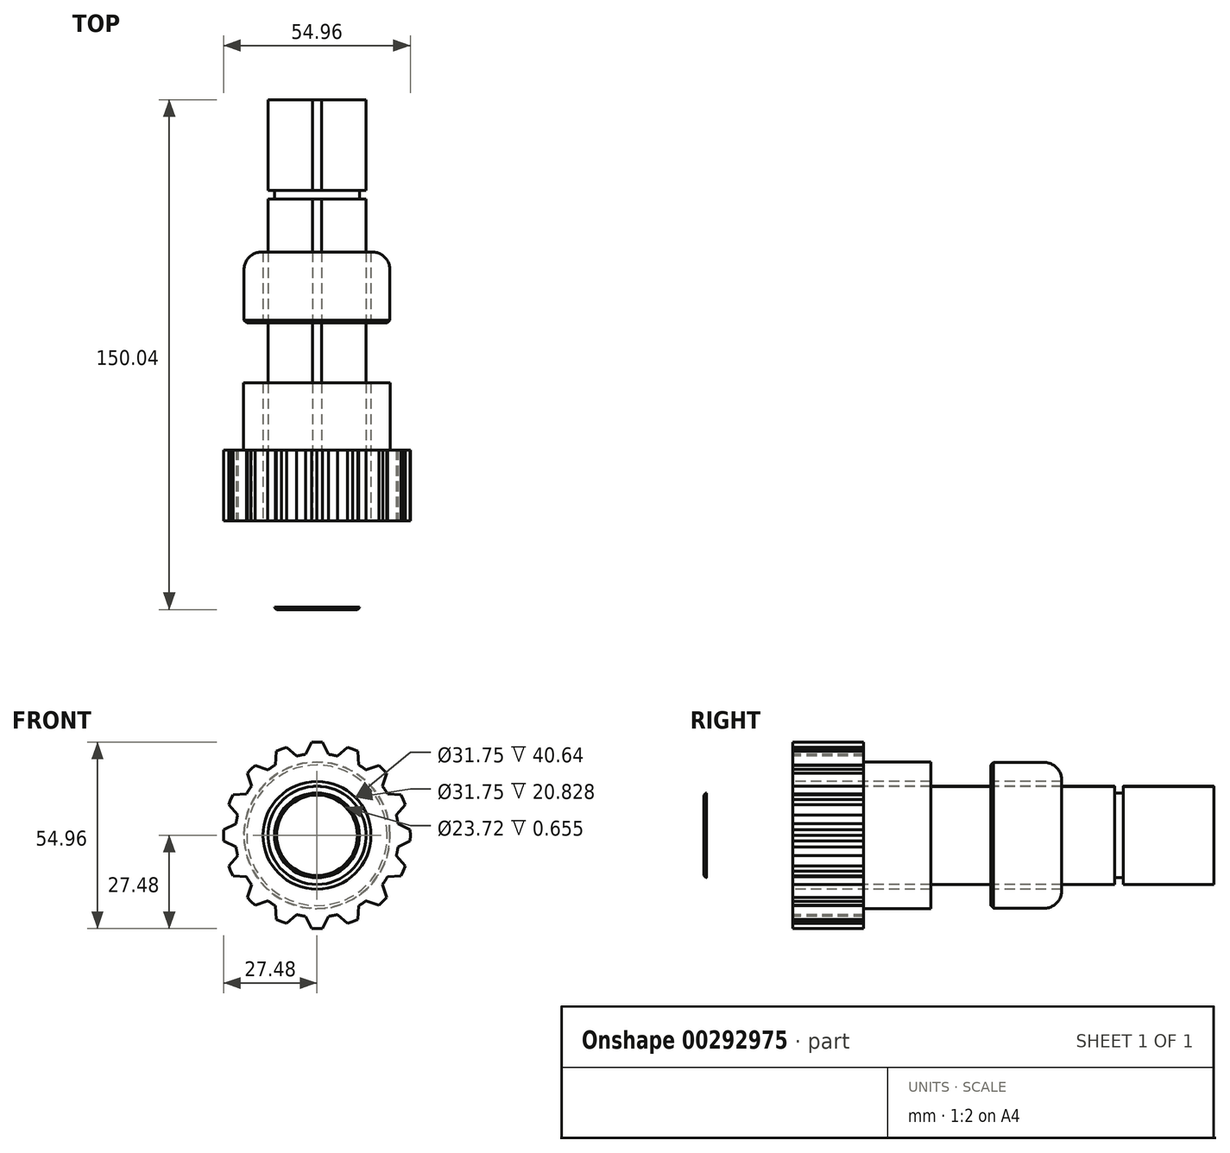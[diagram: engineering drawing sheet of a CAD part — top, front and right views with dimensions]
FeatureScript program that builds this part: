
annotation { "Feature Type Name" : "Feature", "Feature Type Description" : "" }
export const myFeature = defineFeature(function(context is Context, id is Id, definition is map)
    precondition{}
    {
        {
            var Q0;
            Q0=qCreatedBy(makeId("Front.planeOp"),FACE);
            var sketch = newSketch(context, id + "F0", { "sketchPlane" : qUnion([Q0])});
            skCircle(sketch, "E0", {"center": v(0, 0) * mm, "radius": 12.5 * mm});
            skCircle(sketch, "E1", {"center": v(0, 0) * mm, "radius": 15.88 * mm});
            skCircle(sketch, "E2", {"center": v(0, 0) * mm, "radius": 21.46 * mm});
            skCircle(sketch, "E3", {"center": v(0, 0) * mm, "radius": 11.86 * mm});
            skLineSegment(sketch, "E4", {"start": v(0, 15.88) * mm, "end": v(0, 14.45) * mm});
            skCircle(sketch, "E5", {"center": v(0, 0) * mm, "radius": 14.45 * mm});
            skPoint(sketch, "E6", {"position": v(-0.58, 15.85) * mm});
            skPoint(sketch, "E7", {"position": v(-1.3, 14.4) * mm});
            skPoint(sketch, "E8", {"position": v(1.3, 14.4) * mm});
            skPoint(sketch, "E9", {"position": v(0.58, 15.85) * mm});
            skLineSegment(sketch, "E10", {"start": v(-1.3, 14.4) * mm, "end": v(-0.58, 15.85) * mm});
            skLineSegment(sketch, "E11", {"start": v(1.3, 14.4) * mm, "end": v(0.58, 15.85) * mm});
            skLineSegment(sketch, "E12.1.0", {"start": v(-3.41, 15.5) * mm, "end": v(-3.1, 14.11) * mm});
            skLineSegment(sketch, "E12.1.1", {"start": v(-4.36, 13.78) * mm, "end": v(-3.98, 15.35) * mm});
            skLineSegment(sketch, "E12.1.2", {"start": v(-1.83, 14.34) * mm, "end": v(-2.84, 15.6) * mm});
            skLineSegment(sketch, "E12.2.0", {"start": v(-6.67, 14.4) * mm, "end": v(-6.07, 13.12) * mm});
            skLineSegment(sketch, "E12.2.1", {"start": v(-7.22, 12.52) * mm, "end": v(-7.19, 14.14) * mm});
            skLineSegment(sketch, "E12.2.2", {"start": v(-4.87, 13.6) * mm, "end": v(-6.12, 14.63) * mm});
            skLineSegment(sketch, "E13.2.3.0", {"start": v(-9.6, 12.64) * mm, "end": v(-8.75, 11.5) * mm});
            skLineSegment(sketch, "E13.3.3.0", {"start": v(-9.74, 10.67) * mm, "end": v(-10.06, 12.26) * mm});
            skLineSegment(sketch, "E13.6.3.0", {"start": v(-7.68, 12.25) * mm, "end": v(-9.13, 12.97) * mm});
            skLineSegment(sketch, "E13.2.4.0", {"start": v(-12.1, 10.28) * mm, "end": v(-11.02, 9.36) * mm});
            skLineSegment(sketch, "E13.3.4.0", {"start": v(-11.81, 8.33) * mm, "end": v(-12.46, 9.82) * mm});
            skLineSegment(sketch, "E13.6.4.0", {"start": v(-10.13, 10.3) * mm, "end": v(-11.7, 10.7) * mm});
            skLineSegment(sketch, "E13.2.5.0", {"start": v(-14.03, 7.44) * mm, "end": v(-12.77, 6.77) * mm});
            skLineSegment(sketch, "E13.3.5.0", {"start": v(-13.33, 5.6) * mm, "end": v(-14.28, 6.9) * mm});
            skLineSegment(sketch, "E13.6.5.0", {"start": v(-12.1, 7.89) * mm, "end": v(-13.73, 7.94) * mm});
            skLineSegment(sketch, "E13.2.6.0", {"start": v(-15.3, 4.25) * mm, "end": v(-13.93, 3.87) * mm});
            skLineSegment(sketch, "E13.3.6.0", {"start": v(-14.22, 2.6) * mm, "end": v(-15.43, 3.68) * mm});
            skLineSegment(sketch, "E13.6.6.0", {"start": v(-13.52, 5.1) * mm, "end": v(-15.12, 4.8) * mm});
            skLineSegment(sketch, "E13.2.7.0", {"start": v(-15.85, 0.86) * mm, "end": v(-14.43, 0.78) * mm});
            skLineSegment(sketch, "E13.3.7.0", {"start": v(-14.44, -0.52) * mm, "end": v(-15.86, 0.27) * mm});
            skLineSegment(sketch, "E13.6.7.0", {"start": v(-14.3, 2.08) * mm, "end": v(-15.8, 1.44) * mm});
            skLineSegment(sketch, "E13.2.8.0", {"start": v(-15.67, -2.57) * mm, "end": v(-14.26, -2.34) * mm});
            skLineSegment(sketch, "E13.3.8.0", {"start": v(-14, -3.61) * mm, "end": v(-15.55, -3.14) * mm});
            skLineSegment(sketch, "E13.6.8.0", {"start": v(-14.41, -1.05) * mm, "end": v(-15.74, -1.99) * mm});
            skLineSegment(sketch, "E13.2.9.0", {"start": v(-14.75, -5.88) * mm, "end": v(-13.43, -5.35) * mm});
            skLineSegment(sketch, "E13.3.9.0", {"start": v(-12.9, -6.53) * mm, "end": v(-14.5, -6.4) * mm});
            skLineSegment(sketch, "E13.6.9.0", {"start": v(-13.85, -4.12) * mm, "end": v(-14.94, -5.32) * mm});
            skLineSegment(sketch, "E13.2.10.0", {"start": v(-13.14, -8.9) * mm, "end": v(-11.96, -8.11) * mm});
            skLineSegment(sketch, "E13.3.10.0", {"start": v(-11.19, -9.15) * mm, "end": v(-12.8, -9.38) * mm});
            skLineSegment(sketch, "E13.6.10.0", {"start": v(-12.64, -7) * mm, "end": v(-13.45, -8.41) * mm});
            skLineSegment(sketch, "E13.2.11.0", {"start": v(-10.92, -11.53) * mm, "end": v(-9.94, -10.5) * mm});
            skLineSegment(sketch, "E13.3.11.0", {"start": v(-8.96, -11.34) * mm, "end": v(-10.48, -11.9) * mm});
            skLineSegment(sketch, "E13.6.11.0", {"start": v(-10.84, -9.56) * mm, "end": v(-11.32, -11.1) * mm});
            skLineSegment(sketch, "E13.2.12.0", {"start": v(-8.18, -13.6) * mm, "end": v(-7.45, -12.38) * mm});
            skLineSegment(sketch, "E13.3.12.0", {"start": v(-6.3, -13) * mm, "end": v(-7.67, -13.88) * mm});
            skLineSegment(sketch, "E13.6.12.0", {"start": v(-8.53, -11.66) * mm, "end": v(-8.67, -13.28) * mm});
            skLineSegment(sketch, "E13.2.13.0", {"start": v(-5.07, -15.04) * mm, "end": v(-4.61, -13.7) * mm});
            skLineSegment(sketch, "E13.3.13.0", {"start": v(-3.37, -14.06) * mm, "end": v(-4.5, -15.2) * mm});
            skLineSegment(sketch, "E13.6.13.0", {"start": v(-5.83, -13.23) * mm, "end": v(-5.61, -14.83) * mm});
            skLineSegment(sketch, "E13.2.14.0", {"start": v(-1.72, -15.78) * mm, "end": v(-1.56, -14.37) * mm});
            skLineSegment(sketch, "E13.3.14.0", {"start": v(-0.27, -14.45) * mm, "end": v(-1.13, -15.82) * mm});
            skLineSegment(sketch, "E13.6.14.0", {"start": v(-2.85, -14.17) * mm, "end": v(-2.3, -15.7) * mm});
            skLineSegment(sketch, "E13.2.15.0", {"start": v(1.72, -15.78) * mm, "end": v(1.56, -14.37) * mm});
            skLineSegment(sketch, "E13.3.15.0", {"start": v(2.85, -14.17) * mm, "end": v(2.3, -15.7) * mm});
            skLineSegment(sketch, "E13.6.15.0", {"start": v(0.27, -14.45) * mm, "end": v(1.13, -15.82) * mm});
            skLineSegment(sketch, "E13.2.16.0", {"start": v(5.07, -15.04) * mm, "end": v(4.61, -13.7) * mm});
            skLineSegment(sketch, "E13.3.16.0", {"start": v(5.83, -13.23) * mm, "end": v(5.61, -14.83) * mm});
            skLineSegment(sketch, "E13.6.16.0", {"start": v(3.37, -14.06) * mm, "end": v(4.5, -15.2) * mm});
            skLineSegment(sketch, "E13.2.17.0", {"start": v(8.18, -13.6) * mm, "end": v(7.45, -12.38) * mm});
            skLineSegment(sketch, "E13.3.17.0", {"start": v(8.53, -11.66) * mm, "end": v(8.67, -13.28) * mm});
            skLineSegment(sketch, "E13.6.17.0", {"start": v(6.3, -13) * mm, "end": v(7.67, -13.88) * mm});
            skLineSegment(sketch, "E13.2.18.0", {"start": v(10.92, -11.53) * mm, "end": v(9.94, -10.5) * mm});
            skLineSegment(sketch, "E13.3.18.0", {"start": v(10.84, -9.56) * mm, "end": v(11.32, -11.1) * mm});
            skLineSegment(sketch, "E13.6.18.0", {"start": v(8.96, -11.34) * mm, "end": v(10.48, -11.9) * mm});
            skLineSegment(sketch, "E13.2.19.0", {"start": v(13.14, -8.9) * mm, "end": v(11.96, -8.11) * mm});
            skLineSegment(sketch, "E13.3.19.0", {"start": v(12.64, -7) * mm, "end": v(13.45, -8.41) * mm});
            skLineSegment(sketch, "E13.6.19.0", {"start": v(11.19, -9.15) * mm, "end": v(12.8, -9.38) * mm});
            skLineSegment(sketch, "E13.2.20.0", {"start": v(14.75, -5.88) * mm, "end": v(13.43, -5.35) * mm});
            skLineSegment(sketch, "E13.3.20.0", {"start": v(13.85, -4.12) * mm, "end": v(14.94, -5.32) * mm});
            skLineSegment(sketch, "E13.6.20.0", {"start": v(12.9, -6.53) * mm, "end": v(14.5, -6.4) * mm});
            skLineSegment(sketch, "E13.2.21.0", {"start": v(15.67, -2.57) * mm, "end": v(14.26, -2.34) * mm});
            skLineSegment(sketch, "E13.3.21.0", {"start": v(14.41, -1.05) * mm, "end": v(15.74, -1.99) * mm});
            skLineSegment(sketch, "E13.6.21.0", {"start": v(14, -3.61) * mm, "end": v(15.55, -3.14) * mm});
            skLineSegment(sketch, "E13.2.22.0", {"start": v(15.85, 0.86) * mm, "end": v(14.43, 0.78) * mm});
            skLineSegment(sketch, "E13.3.22.0", {"start": v(14.3, 2.08) * mm, "end": v(15.8, 1.44) * mm});
            skLineSegment(sketch, "E13.6.22.0", {"start": v(14.44, -0.52) * mm, "end": v(15.86, 0.27) * mm});
            skLineSegment(sketch, "E13.2.23.0", {"start": v(15.3, 4.25) * mm, "end": v(13.93, 3.87) * mm});
            skLineSegment(sketch, "E13.3.23.0", {"start": v(13.52, 5.1) * mm, "end": v(15.12, 4.8) * mm});
            skLineSegment(sketch, "E13.6.23.0", {"start": v(14.22, 2.6) * mm, "end": v(15.43, 3.68) * mm});
            skLineSegment(sketch, "E13.2.24.0", {"start": v(14.03, 7.44) * mm, "end": v(12.77, 6.77) * mm});
            skLineSegment(sketch, "E13.3.24.0", {"start": v(12.1, 7.89) * mm, "end": v(13.73, 7.94) * mm});
            skLineSegment(sketch, "E13.6.24.0", {"start": v(13.33, 5.6) * mm, "end": v(14.28, 6.9) * mm});
            skLineSegment(sketch, "E13.2.25.0", {"start": v(12.1, 10.28) * mm, "end": v(11.02, 9.36) * mm});
            skLineSegment(sketch, "E13.3.25.0", {"start": v(10.13, 10.3) * mm, "end": v(11.7, 10.7) * mm});
            skLineSegment(sketch, "E13.6.25.0", {"start": v(11.81, 8.33) * mm, "end": v(12.46, 9.82) * mm});
            skLineSegment(sketch, "E13.2.26.0", {"start": v(9.6, 12.64) * mm, "end": v(8.75, 11.5) * mm});
            skLineSegment(sketch, "E13.3.26.0", {"start": v(7.68, 12.25) * mm, "end": v(9.13, 12.97) * mm});
            skLineSegment(sketch, "E13.6.26.0", {"start": v(9.74, 10.67) * mm, "end": v(10.06, 12.26) * mm});
            skLineSegment(sketch, "E13.2.27.0", {"start": v(6.67, 14.4) * mm, "end": v(6.07, 13.12) * mm});
            skLineSegment(sketch, "E13.3.27.0", {"start": v(4.87, 13.6) * mm, "end": v(6.12, 14.63) * mm});
            skLineSegment(sketch, "E13.6.27.0", {"start": v(7.22, 12.52) * mm, "end": v(7.19, 14.14) * mm});
            skLineSegment(sketch, "E13.2.28.0", {"start": v(3.41, 15.5) * mm, "end": v(3.1, 14.11) * mm});
            skLineSegment(sketch, "E13.3.28.0", {"start": v(1.83, 14.34) * mm, "end": v(2.84, 15.6) * mm});
            skLineSegment(sketch, "E13.6.28.0", {"start": v(4.36, 13.78) * mm, "end": v(3.98, 15.35) * mm});
            skFitSpline(sketch, "E14", {"points": [v(-1.3, 14.4) * mm, v(0, 14.45) * mm, v(1.3, 14.4) * mm], "startDerivative": vector(2.6, 0.18) * mm, "endDerivative": vector(2.6, -0.18) * mm});
            skFitSpline(sketch, "E15", {"points": [v(-0.58, 15.85) * mm, v(0, 15.88) * mm, v(0.58, 15.85) * mm], "startDerivative": vector(1.17, 0.08) * mm, "endDerivative": vector(1.17, -0.08) * mm});
            skSolve(sketch);
        }
        {
            var Q0;
            Q0=makeQuery(id+"F0.imprint","IMPRINT",FACE,{"disambiguationData":[TD([[makeQuery(id+"F0.imprint","IMPRINT",EDGE,{"derivedFrom":sQuery(id+"F0.wireOp",EDGE,"E0")}),1.0]])]});
            extrude(context, id + "F1", {"entities" : qUnion([Q0]), "depth" : 26.21 * mm, "hasSecondDirection" : true, "secondDirectionOppositeDirection" : false, "secondDirectionDepth" : 25.4 * mm});
        }
        {
            var Q0;
            Q0=makeQuery(id+"F0.imprint","IMPRINT",FACE,{"disambiguationData":[TD([[makeQuery(id+"F0.imprint","IMPRINT",EDGE,{"derivedFrom":sQuery(id+"F0.wireOp",EDGE,"E0")}),1.0]])]});
            extrude(context, id + "F2", {"entities" : qUnion([Q0]), "operationType" : NewBodyOperationType.REMOVE, "depth" : 1.47 * mm});
        }
        {
            var Q0;
            Q0=makeQuery(id+"F0.imprint","IMPRINT",FACE,{"disambiguationData":[TD([[makeQuery(id+"F0.imprint","IMPRINT",EDGE,{"derivedFrom":sQuery(id+"F0.wireOp",EDGE,"E3")}),1.0]])]});
            var Q1;
            Q1=makeQuery(id+"F0.imprint","IMPRINT",FACE,{"disambiguationData":[TD([[makeQuery(id+"F0.imprint","IMPRINT",EDGE,{"derivedFrom":sQuery(id+"F0.wireOp",EDGE,"E0")}),1.0]])]});
            var Q2;
            Q2=makeQuery(id+"F0.imprint","IMPRINT",FACE,{"disambiguationData":[TD([[makeQuery(id+"F0.imprint","IMPRINT",EDGE,{"derivedFrom":sQuery(id+"F0.wireOp",EDGE,"E0")}),-1.0]])]});
            extrude(context, id + "F3", {"entities" : qUnion([Q0, Q1, Q2]), "operationType" : NewBodyOperationType.ADD, "oppositeDirection" : true, "depth" : 123.98 * mm});
        }
        {
            var Q0;
            Q0=makeQuery(id+"F0.imprint","IMPRINT",FACE,{"disambiguationData":[TD([[makeQuery(id+"F0.imprint","IMPRINT",EDGE,{"derivedFrom":sQuery(id+"F0.wireOp",EDGE,"E0")}),-1.0]])]});
            extrude(context, id + "F4", {"entities" : qUnion([Q0]), "operationType" : NewBodyOperationType.REMOVE, "oppositeDirection" : true, "depth" : 97.3 * mm, "hasSecondDirection" : true, "secondDirectionOppositeDirection" : true, "secondDirectionDepth" : 94.77 * mm});
        }
        {
            var Q0;
            Q0=makeQuery(id+"F0.imprint","IMPRINT",FACE,{"disambiguationData":[TD([[makeQuery(id+"F0.imprint","IMPRINT",EDGE,{"derivedFrom":sQuery(id+"F0.wireOp",EDGE,"E1")}),-1.0]])]});
            extrude(context, id + "F5", {"entities" : qUnion([Q0]), "operationType" : NewBodyOperationType.ADD, "oppositeDirection" : true, "depth" : 79.2 * mm, "hasSecondDirection" : true, "secondDirectionOppositeDirection" : true, "secondDirectionDepth" : 58.37 * mm});
        }
        {
            var Q0;
            Q0=makeQuery(id+"F1.opExtrude","CAP_EDGE",EDGE,{"disambiguationData":[OSD([sQuery(id+"F0.wireOp",EDGE,"E0")])],"isStart":false});
            chamfer(context, id + "F6", {"entities" : qUnion([Q0]), "width" : 0.8 * mm, "tangentPropagation" : true});
        }
        {
            var Q0;
            Q0=makeQuery(id+"F5.opExtrude","CAP_EDGE",EDGE,{"disambiguationData":[OSD([sQuery(id+"F0.wireOp",EDGE,"E2")])],"isStart":false});
            fillet(context, id + "F7", {"entities" : qUnion([Q0]), "radius" : 5.16 * mm, "tangentPropagation" : true, "allowEdgeOverflow" : false});
        }
        {
            var Q0;
            Q0=makeQuery(id+"F5.opExtrude","CAP_EDGE",EDGE,{"disambiguationData":[OSD([sQuery(id+"F0.wireOp",EDGE,"E2")])],"isStart":true});
            chamfer(context, id + "F8", {"entities" : qUnion([Q0]), "width" : 0.79 * mm, "tangentPropagation" : true});
        }
        {
            var Q0;
            Q0=qCreatedBy(makeId("Front.planeOp"),FACE);
            var sketch = newSketch(context, id + "F9", { "sketchPlane" : qUnion([Q0])});
            skCircle(sketch, "E16", {"center": v(0, 0) * mm, "radius": 15.88 * mm});
            skCircle(sketch, "E17", {"center": v(0, 0) * mm, "radius": 21.6 * mm});
            skLineSegment(sketch, "E18", {"start": v(0, 27.48) * mm, "end": v(1.62, 27.43) * mm});
            skLineSegment(sketch, "E19", {"start": v(0, 27.48) * mm, "end": v(-1.62, 27.43) * mm});
            skLineSegment(sketch, "E20", {"start": v(0, 27.48) * mm, "end": v(0, 24.09) * mm});
            skLineSegment(sketch, "E21", {"start": v(-3.37, 23.85) * mm, "end": v(-1.62, 27.43) * mm});
            skLineSegment(sketch, "E22", {"start": v(3.37, 23.85) * mm, "end": v(1.62, 27.43) * mm});
            skLineSegment(sketch, "E23.1.0", {"start": v(-12.24, 20.74) * mm, "end": v(-12, 24.72) * mm});
            skLineSegment(sketch, "E23.1.1", {"start": v(-10.52, 25.39) * mm, "end": v(-9.22, 22.25) * mm});
            skLineSegment(sketch, "E23.1.4", {"start": v(-6.01, 23.32) * mm, "end": v(-9, 25.96) * mm});
            skLineSegment(sketch, "E23.1.5", {"start": v(-10.52, 25.39) * mm, "end": v(-9, 25.96) * mm});
            skLineSegment(sketch, "E23.1.6", {"start": v(-10.52, 25.39) * mm, "end": v(-12, 24.72) * mm});
            skLineSegment(sketch, "E23.2.0", {"start": v(-19.25, 14.48) * mm, "end": v(-20.54, 18.25) * mm});
            skLineSegment(sketch, "E23.2.1", {"start": v(-19.43, 19.43) * mm, "end": v(-17.03, 17.03) * mm});
            skLineSegment(sketch, "E23.2.4", {"start": v(-14.48, 19.25) * mm, "end": v(-18.25, 20.54) * mm});
            skLineSegment(sketch, "E23.2.5", {"start": v(-19.43, 19.43) * mm, "end": v(-18.25, 20.54) * mm});
            skLineSegment(sketch, "E23.2.6", {"start": v(-19.43, 19.43) * mm, "end": v(-20.54, 18.25) * mm});
            skLineSegment(sketch, "E24.1.3.0", {"start": v(-23.32, 6.01) * mm, "end": v(-25.96, 9) * mm});
            skLineSegment(sketch, "E24.3.3.0", {"start": v(-25.39, 10.52) * mm, "end": v(-22.25, 9.22) * mm});
            skLineSegment(sketch, "E24.12.3.0", {"start": v(-20.74, 12.24) * mm, "end": v(-24.72, 12) * mm});
            skLineSegment(sketch, "E24.15.3.0", {"start": v(-25.39, 10.52) * mm, "end": v(-24.72, 12) * mm});
            skLineSegment(sketch, "E24.18.3.0", {"start": v(-25.39, 10.52) * mm, "end": v(-25.96, 9) * mm});
            skLineSegment(sketch, "E24.1.4.0", {"start": v(-23.85, -3.37) * mm, "end": v(-27.43, -1.62) * mm});
            skLineSegment(sketch, "E24.3.4.0", {"start": v(-27.48, 0) * mm, "end": v(-24.09, 0) * mm});
            skLineSegment(sketch, "E24.12.4.0", {"start": v(-23.85, 3.37) * mm, "end": v(-27.43, 1.62) * mm});
            skLineSegment(sketch, "E24.15.4.0", {"start": v(-27.48, 0) * mm, "end": v(-27.43, 1.62) * mm});
            skLineSegment(sketch, "E24.18.4.0", {"start": v(-27.48, 0) * mm, "end": v(-27.43, -1.62) * mm});
            skLineSegment(sketch, "E24.1.5.0", {"start": v(-20.74, -12.24) * mm, "end": v(-24.72, -12) * mm});
            skLineSegment(sketch, "E24.3.5.0", {"start": v(-25.39, -10.52) * mm, "end": v(-22.25, -9.22) * mm});
            skLineSegment(sketch, "E24.12.5.0", {"start": v(-23.32, -6.01) * mm, "end": v(-25.96, -9) * mm});
            skLineSegment(sketch, "E24.15.5.0", {"start": v(-25.39, -10.52) * mm, "end": v(-25.96, -9) * mm});
            skLineSegment(sketch, "E24.18.5.0", {"start": v(-25.39, -10.52) * mm, "end": v(-24.72, -12) * mm});
            skLineSegment(sketch, "E24.1.6.0", {"start": v(-14.48, -19.25) * mm, "end": v(-18.25, -20.54) * mm});
            skLineSegment(sketch, "E24.3.6.0", {"start": v(-19.43, -19.43) * mm, "end": v(-17.03, -17.03) * mm});
            skLineSegment(sketch, "E24.12.6.0", {"start": v(-19.25, -14.48) * mm, "end": v(-20.54, -18.25) * mm});
            skLineSegment(sketch, "E24.15.6.0", {"start": v(-19.43, -19.43) * mm, "end": v(-20.54, -18.25) * mm});
            skLineSegment(sketch, "E24.18.6.0", {"start": v(-19.43, -19.43) * mm, "end": v(-18.25, -20.54) * mm});
            skLineSegment(sketch, "E24.1.7.0", {"start": v(-6.01, -23.32) * mm, "end": v(-9, -25.96) * mm});
            skLineSegment(sketch, "E24.3.7.0", {"start": v(-10.52, -25.39) * mm, "end": v(-9.22, -22.25) * mm});
            skLineSegment(sketch, "E24.12.7.0", {"start": v(-12.24, -20.74) * mm, "end": v(-12, -24.72) * mm});
            skLineSegment(sketch, "E24.15.7.0", {"start": v(-10.52, -25.39) * mm, "end": v(-12, -24.72) * mm});
            skLineSegment(sketch, "E24.18.7.0", {"start": v(-10.52, -25.39) * mm, "end": v(-9, -25.96) * mm});
            skLineSegment(sketch, "E24.1.8.0", {"start": v(3.37, -23.85) * mm, "end": v(1.62, -27.43) * mm});
            skLineSegment(sketch, "E24.3.8.0", {"start": v(0, -27.48) * mm, "end": v(0, -24.09) * mm});
            skLineSegment(sketch, "E24.12.8.0", {"start": v(-3.37, -23.85) * mm, "end": v(-1.62, -27.43) * mm});
            skLineSegment(sketch, "E24.15.8.0", {"start": v(0, -27.48) * mm, "end": v(-1.62, -27.43) * mm});
            skLineSegment(sketch, "E24.18.8.0", {"start": v(0, -27.48) * mm, "end": v(1.62, -27.43) * mm});
            skLineSegment(sketch, "E24.1.9.0", {"start": v(12.24, -20.74) * mm, "end": v(12, -24.72) * mm});
            skLineSegment(sketch, "E24.3.9.0", {"start": v(10.52, -25.39) * mm, "end": v(9.22, -22.25) * mm});
            skLineSegment(sketch, "E24.12.9.0", {"start": v(6.01, -23.32) * mm, "end": v(9, -25.96) * mm});
            skLineSegment(sketch, "E24.15.9.0", {"start": v(10.52, -25.39) * mm, "end": v(9, -25.96) * mm});
            skLineSegment(sketch, "E24.18.9.0", {"start": v(10.52, -25.39) * mm, "end": v(12, -24.72) * mm});
            skLineSegment(sketch, "E24.1.10.0", {"start": v(19.25, -14.48) * mm, "end": v(20.54, -18.25) * mm});
            skLineSegment(sketch, "E24.3.10.0", {"start": v(19.43, -19.43) * mm, "end": v(17.03, -17.03) * mm});
            skLineSegment(sketch, "E24.12.10.0", {"start": v(14.48, -19.25) * mm, "end": v(18.25, -20.54) * mm});
            skLineSegment(sketch, "E24.15.10.0", {"start": v(19.43, -19.43) * mm, "end": v(18.25, -20.54) * mm});
            skLineSegment(sketch, "E24.18.10.0", {"start": v(19.43, -19.43) * mm, "end": v(20.54, -18.25) * mm});
            skLineSegment(sketch, "E24.1.11.0", {"start": v(23.32, -6.01) * mm, "end": v(25.96, -9) * mm});
            skLineSegment(sketch, "E24.3.11.0", {"start": v(25.39, -10.52) * mm, "end": v(22.25, -9.22) * mm});
            skLineSegment(sketch, "E24.12.11.0", {"start": v(20.74, -12.24) * mm, "end": v(24.72, -12) * mm});
            skLineSegment(sketch, "E24.15.11.0", {"start": v(25.39, -10.52) * mm, "end": v(24.72, -12) * mm});
            skLineSegment(sketch, "E24.18.11.0", {"start": v(25.39, -10.52) * mm, "end": v(25.96, -9) * mm});
            skLineSegment(sketch, "E24.1.12.0", {"start": v(23.85, 3.37) * mm, "end": v(27.43, 1.62) * mm});
            skLineSegment(sketch, "E24.3.12.0", {"start": v(27.48, 0) * mm, "end": v(24.09, 0) * mm});
            skLineSegment(sketch, "E24.12.12.0", {"start": v(23.85, -3.37) * mm, "end": v(27.43, -1.62) * mm});
            skLineSegment(sketch, "E24.15.12.0", {"start": v(27.48, 0) * mm, "end": v(27.43, -1.62) * mm});
            skLineSegment(sketch, "E24.18.12.0", {"start": v(27.48, 0) * mm, "end": v(27.43, 1.62) * mm});
            skLineSegment(sketch, "E24.1.13.0", {"start": v(20.74, 12.24) * mm, "end": v(24.72, 12) * mm});
            skLineSegment(sketch, "E24.3.13.0", {"start": v(25.39, 10.52) * mm, "end": v(22.25, 9.22) * mm});
            skLineSegment(sketch, "E24.12.13.0", {"start": v(23.32, 6.01) * mm, "end": v(25.96, 9) * mm});
            skLineSegment(sketch, "E24.15.13.0", {"start": v(25.39, 10.52) * mm, "end": v(25.96, 9) * mm});
            skLineSegment(sketch, "E24.18.13.0", {"start": v(25.39, 10.52) * mm, "end": v(24.72, 12) * mm});
            skLineSegment(sketch, "E24.1.14.0", {"start": v(14.48, 19.25) * mm, "end": v(18.25, 20.54) * mm});
            skLineSegment(sketch, "E24.3.14.0", {"start": v(19.43, 19.43) * mm, "end": v(17.03, 17.03) * mm});
            skLineSegment(sketch, "E24.12.14.0", {"start": v(19.25, 14.48) * mm, "end": v(20.54, 18.25) * mm});
            skLineSegment(sketch, "E24.15.14.0", {"start": v(19.43, 19.43) * mm, "end": v(20.54, 18.25) * mm});
            skLineSegment(sketch, "E24.18.14.0", {"start": v(19.43, 19.43) * mm, "end": v(18.25, 20.54) * mm});
            skLineSegment(sketch, "E24.1.15.0", {"start": v(6.01, 23.32) * mm, "end": v(9, 25.96) * mm});
            skLineSegment(sketch, "E24.3.15.0", {"start": v(10.52, 25.39) * mm, "end": v(9.22, 22.25) * mm});
            skLineSegment(sketch, "E24.12.15.0", {"start": v(12.24, 20.74) * mm, "end": v(12, 24.72) * mm});
            skLineSegment(sketch, "E24.15.15.0", {"start": v(10.52, 25.39) * mm, "end": v(12, 24.72) * mm});
            skLineSegment(sketch, "E24.18.15.0", {"start": v(10.52, 25.39) * mm, "end": v(9, 25.96) * mm});
            skCircle(sketch, "E25", {"center": v(0, 0) * mm, "radius": 24.09 * mm});
            skCircle(sketch, "E26", {"center": v(0, 0) * mm, "radius": 27.48 * mm});
            skSolve(sketch);
        }
        {
            var Q0;
            Q0=makeQuery(id+"F9.imprint","IMPRINT",FACE,{"disambiguationData":[TD([[makeQuery(id+"F9.imprint","IMPRINT",EDGE,{"derivedFrom":sQuery(id+"F9.wireOp",EDGE,"E16")}),-1.0]])]});
            extrude(context, id + "F10", {"entities" : qUnion([Q0]), "oppositeDirection" : true, "depth" : 40.64 * mm});
        }
        {
            var Q0;
            Q0=makeQuery(id+"F9.imprint","IMPRINT",FACE,{"disambiguationData":[TD([[makeQuery(id+"F9.imprint","IMPRINT",EDGE,{"derivedFrom":sQuery(id+"F9.wireOp",EDGE,"E17")}),-1.0]])]});
            var Q1;
            {var subQ0=sQuery(id+"F9.wireOp",EDGE,"E24.1.15.0");Q1=makeQuery(id+"F9.imprint","IMPRINT",FACE,{"disambiguationData":[TD([[makeQuery(id+"F9.imprint","IMPRINT",EDGE,{"derivedFrom":subQ0}),-1.0]])]});}
            var Q2;
            {var subQ0=sQuery(id+"F9.wireOp",EDGE,"E24.3.15.0");Q2=makeQuery(id+"F9.imprint","IMPRINT",FACE,{"disambiguationData":[TD([[makeQuery(id+"F9.imprint","IMPRINT",EDGE,{"derivedFrom":subQ0}),1.0]])]});}
            var Q3;
            {var subQ0=sQuery(id+"F9.wireOp",EDGE,"E24.1.14.0");Q3=makeQuery(id+"F9.imprint","IMPRINT",FACE,{"disambiguationData":[TD([[makeQuery(id+"F9.imprint","IMPRINT",EDGE,{"derivedFrom":subQ0}),-1.0]])]});}
            var Q4;
            {var subQ0=sQuery(id+"F9.wireOp",EDGE,"E24.3.14.0");Q4=makeQuery(id+"F9.imprint","IMPRINT",FACE,{"disambiguationData":[TD([[makeQuery(id+"F9.imprint","IMPRINT",EDGE,{"derivedFrom":subQ0}),1.0]])]});}
            var Q5;
            {var subQ0=sQuery(id+"F9.wireOp",EDGE,"E24.1.13.0");Q5=makeQuery(id+"F9.imprint","IMPRINT",FACE,{"disambiguationData":[TD([[makeQuery(id+"F9.imprint","IMPRINT",EDGE,{"derivedFrom":subQ0}),-1.0]])]});}
            var Q6;
            {var subQ0=sQuery(id+"F9.wireOp",EDGE,"E24.3.13.0");Q6=makeQuery(id+"F9.imprint","IMPRINT",FACE,{"disambiguationData":[TD([[makeQuery(id+"F9.imprint","IMPRINT",EDGE,{"derivedFrom":subQ0}),1.0]])]});}
            var Q7;
            {var subQ0=sQuery(id+"F9.wireOp",EDGE,"E24.1.12.0");Q7=makeQuery(id+"F9.imprint","IMPRINT",FACE,{"disambiguationData":[TD([[makeQuery(id+"F9.imprint","IMPRINT",EDGE,{"derivedFrom":subQ0}),-1.0]])]});}
            var Q8;
            {var subQ0=sQuery(id+"F9.wireOp",EDGE,"E24.3.12.0");Q8=makeQuery(id+"F9.imprint","IMPRINT",FACE,{"disambiguationData":[TD([[makeQuery(id+"F9.imprint","IMPRINT",EDGE,{"derivedFrom":subQ0}),1.0]])]});}
            var Q9;
            {var subQ0=sQuery(id+"F9.wireOp",EDGE,"E24.1.11.0");Q9=makeQuery(id+"F9.imprint","IMPRINT",FACE,{"disambiguationData":[TD([[makeQuery(id+"F9.imprint","IMPRINT",EDGE,{"derivedFrom":subQ0}),-1.0]])]});}
            var Q10;
            {var subQ0=sQuery(id+"F9.wireOp",EDGE,"E24.3.11.0");Q10=makeQuery(id+"F9.imprint","IMPRINT",FACE,{"disambiguationData":[TD([[makeQuery(id+"F9.imprint","IMPRINT",EDGE,{"derivedFrom":subQ0}),1.0]])]});}
            var Q11;
            {var subQ0=sQuery(id+"F9.wireOp",EDGE,"E24.1.10.0");Q11=makeQuery(id+"F9.imprint","IMPRINT",FACE,{"disambiguationData":[TD([[makeQuery(id+"F9.imprint","IMPRINT",EDGE,{"derivedFrom":subQ0}),-1.0]])]});}
            var Q12;
            {var subQ0=sQuery(id+"F9.wireOp",EDGE,"E24.3.10.0");Q12=makeQuery(id+"F9.imprint","IMPRINT",FACE,{"disambiguationData":[TD([[makeQuery(id+"F9.imprint","IMPRINT",EDGE,{"derivedFrom":subQ0}),1.0]])]});}
            var Q13;
            {var subQ0=sQuery(id+"F9.wireOp",EDGE,"E24.1.9.0");Q13=makeQuery(id+"F9.imprint","IMPRINT",FACE,{"disambiguationData":[TD([[makeQuery(id+"F9.imprint","IMPRINT",EDGE,{"derivedFrom":subQ0}),-1.0]])]});}
            var Q14;
            {var subQ0=sQuery(id+"F9.wireOp",EDGE,"E24.3.9.0");Q14=makeQuery(id+"F9.imprint","IMPRINT",FACE,{"disambiguationData":[TD([[makeQuery(id+"F9.imprint","IMPRINT",EDGE,{"derivedFrom":subQ0}),1.0]])]});}
            var Q15;
            {var subQ0=sQuery(id+"F9.wireOp",EDGE,"E24.1.8.0");Q15=makeQuery(id+"F9.imprint","IMPRINT",FACE,{"disambiguationData":[TD([[makeQuery(id+"F9.imprint","IMPRINT",EDGE,{"derivedFrom":subQ0}),-1.0]])]});}
            var Q16;
            {var subQ0=sQuery(id+"F9.wireOp",EDGE,"E24.3.8.0");Q16=makeQuery(id+"F9.imprint","IMPRINT",FACE,{"disambiguationData":[TD([[makeQuery(id+"F9.imprint","IMPRINT",EDGE,{"derivedFrom":subQ0}),1.0]])]});}
            var Q17;
            {var subQ0=sQuery(id+"F9.wireOp",EDGE,"E24.1.7.0");Q17=makeQuery(id+"F9.imprint","IMPRINT",FACE,{"disambiguationData":[TD([[makeQuery(id+"F9.imprint","IMPRINT",EDGE,{"derivedFrom":subQ0}),-1.0]])]});}
            var Q18;
            {var subQ0=sQuery(id+"F9.wireOp",EDGE,"E24.3.7.0");Q18=makeQuery(id+"F9.imprint","IMPRINT",FACE,{"disambiguationData":[TD([[makeQuery(id+"F9.imprint","IMPRINT",EDGE,{"derivedFrom":subQ0}),1.0]])]});}
            var Q19;
            {var subQ0=sQuery(id+"F9.wireOp",EDGE,"E24.1.6.0");Q19=makeQuery(id+"F9.imprint","IMPRINT",FACE,{"disambiguationData":[TD([[makeQuery(id+"F9.imprint","IMPRINT",EDGE,{"derivedFrom":subQ0}),-1.0]])]});}
            var Q20;
            {var subQ0=sQuery(id+"F9.wireOp",EDGE,"E24.3.6.0");Q20=makeQuery(id+"F9.imprint","IMPRINT",FACE,{"disambiguationData":[TD([[makeQuery(id+"F9.imprint","IMPRINT",EDGE,{"derivedFrom":subQ0}),1.0]])]});}
            var Q21;
            {var subQ0=sQuery(id+"F9.wireOp",EDGE,"E24.1.5.0");Q21=makeQuery(id+"F9.imprint","IMPRINT",FACE,{"disambiguationData":[TD([[makeQuery(id+"F9.imprint","IMPRINT",EDGE,{"derivedFrom":subQ0}),-1.0]])]});}
            var Q22;
            {var subQ0=sQuery(id+"F9.wireOp",EDGE,"E24.3.5.0");Q22=makeQuery(id+"F9.imprint","IMPRINT",FACE,{"disambiguationData":[TD([[makeQuery(id+"F9.imprint","IMPRINT",EDGE,{"derivedFrom":subQ0}),1.0]])]});}
            var Q23;
            {var subQ0=sQuery(id+"F9.wireOp",EDGE,"E24.1.4.0");Q23=makeQuery(id+"F9.imprint","IMPRINT",FACE,{"disambiguationData":[TD([[makeQuery(id+"F9.imprint","IMPRINT",EDGE,{"derivedFrom":subQ0}),-1.0]])]});}
            var Q24;
            {var subQ0=sQuery(id+"F9.wireOp",EDGE,"E24.3.4.0");Q24=makeQuery(id+"F9.imprint","IMPRINT",FACE,{"disambiguationData":[TD([[makeQuery(id+"F9.imprint","IMPRINT",EDGE,{"derivedFrom":subQ0}),1.0]])]});}
            var Q25;
            {var subQ0=sQuery(id+"F9.wireOp",EDGE,"E24.1.3.0");Q25=makeQuery(id+"F9.imprint","IMPRINT",FACE,{"disambiguationData":[TD([[makeQuery(id+"F9.imprint","IMPRINT",EDGE,{"derivedFrom":subQ0}),-1.0]])]});}
            var Q26;
            {var subQ0=sQuery(id+"F9.wireOp",EDGE,"E24.3.3.0");Q26=makeQuery(id+"F9.imprint","IMPRINT",FACE,{"disambiguationData":[TD([[makeQuery(id+"F9.imprint","IMPRINT",EDGE,{"derivedFrom":subQ0}),1.0]])]});}
            var Q27;
            {var subQ0=sQuery(id+"F9.wireOp",EDGE,"E23.2.0");Q27=makeQuery(id+"F9.imprint","IMPRINT",FACE,{"disambiguationData":[TD([[makeQuery(id+"F9.imprint","IMPRINT",EDGE,{"derivedFrom":subQ0}),-1.0]])]});}
            var Q28;
            {var subQ0=sQuery(id+"F9.wireOp",EDGE,"E23.2.1");Q28=makeQuery(id+"F9.imprint","IMPRINT",FACE,{"disambiguationData":[TD([[makeQuery(id+"F9.imprint","IMPRINT",EDGE,{"derivedFrom":subQ0}),1.0]])]});}
            var Q29;
            {var subQ0=sQuery(id+"F9.wireOp",EDGE,"E23.1.0");Q29=makeQuery(id+"F9.imprint","IMPRINT",FACE,{"disambiguationData":[TD([[makeQuery(id+"F9.imprint","IMPRINT",EDGE,{"derivedFrom":subQ0}),-1.0]])]});}
            var Q30;
            {var subQ0=sQuery(id+"F9.wireOp",EDGE,"E23.1.1");Q30=makeQuery(id+"F9.imprint","IMPRINT",FACE,{"disambiguationData":[TD([[makeQuery(id+"F9.imprint","IMPRINT",EDGE,{"derivedFrom":subQ0}),1.0]])]});}
            var Q31;
            Q31=makeQuery(id+"F9.imprint","IMPRINT",FACE,{"disambiguationData":[TD([[makeQuery(id+"F9.imprint","IMPRINT",EDGE,{"derivedFrom":sQuery(id+"F9.wireOp",EDGE,"E19")}),1.0]])]});
            var Q32;
            Q32=makeQuery(id+"F9.imprint","IMPRINT",FACE,{"disambiguationData":[TD([[makeQuery(id+"F9.imprint","IMPRINT",EDGE,{"derivedFrom":sQuery(id+"F9.wireOp",EDGE,"E18")}),-1.0]])]});
            extrude(context, id + "F11", {"entities" : qUnion([Q0, Q1, Q2, Q3, Q4, Q5, Q6, Q7, Q8, Q9, Q10, Q11, Q12, Q13, Q14, Q15, Q16, Q17, Q18, Q19, Q20, Q21, Q22, Q23, Q24, Q25, Q26, Q27, Q28, Q29, Q30, Q31, Q32]), "operationType" : NewBodyOperationType.ADD, "oppositeDirection" : true, "depth" : 20.9 * mm});
        }
    });
